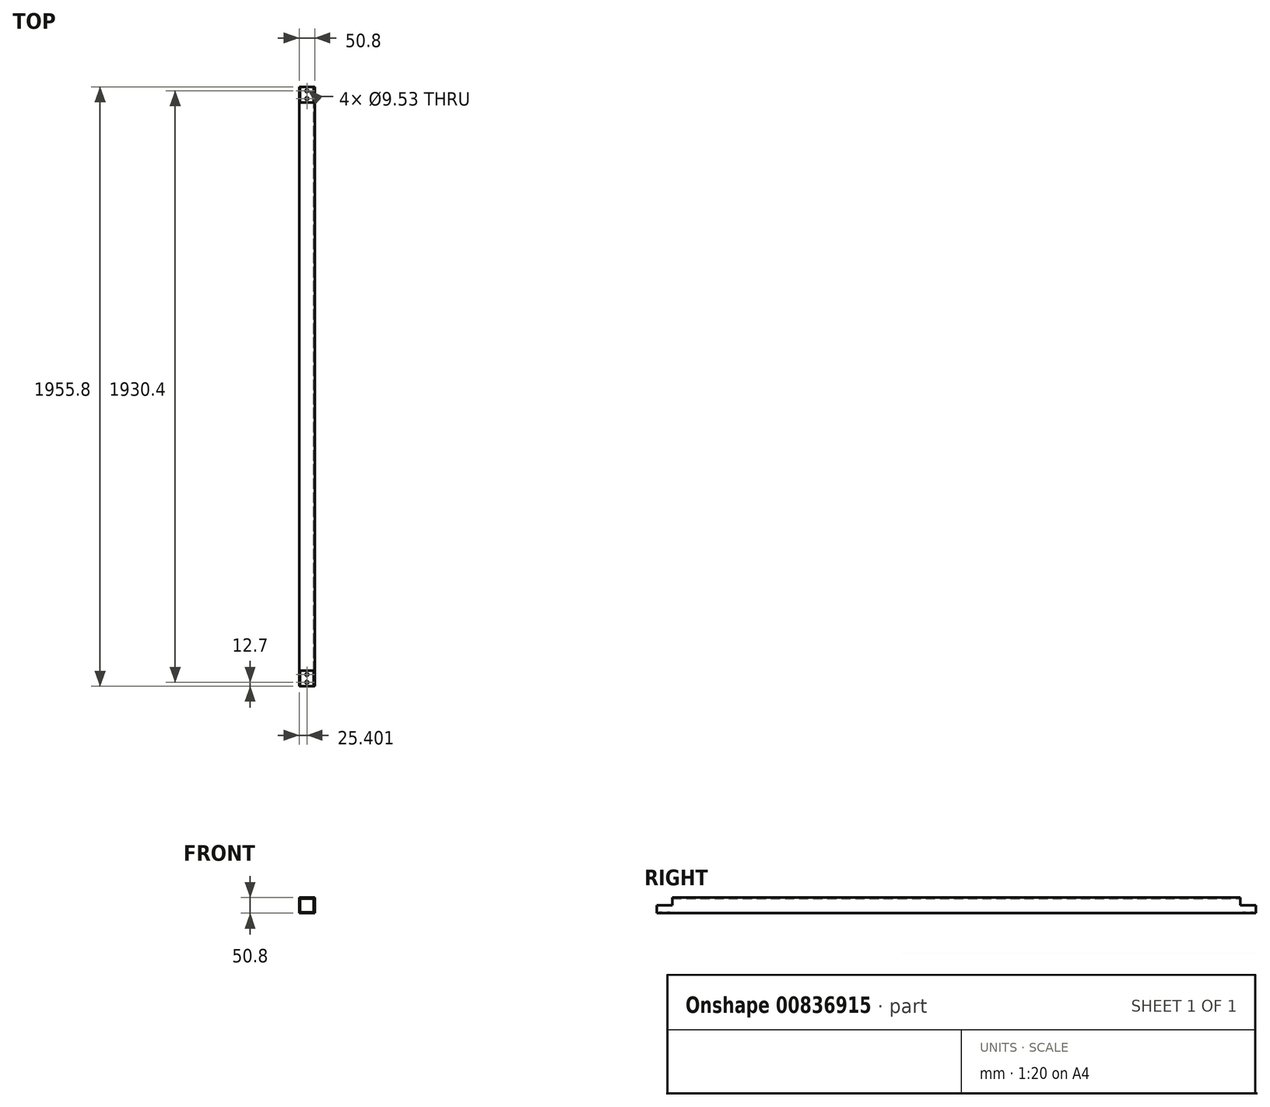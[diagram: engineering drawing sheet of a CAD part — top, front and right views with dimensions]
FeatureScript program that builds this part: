
annotation { "Feature Type Name" : "Feature", "Feature Type Description" : "" }
export const myFeature = defineFeature(function(context is Context, id is Id, definition is map)
    precondition{}
    {
        {
            var Q0;
            Q0=qCreatedBy(makeId("Front.planeOp"),FACE);
            var sketch = newSketch(context, id + "F0", { "sketchPlane" : qUnion([Q0])});
            skLineSegment(sketch, "E0.bottom", {"start": v(-6.18, -7.03) * mm, "end": v(44.62, -7.03) * mm});
            skLineSegment(sketch, "E0.top", {"start": v(-6.18, 43.77) * mm, "end": v(44.62, 43.77) * mm});
            skLineSegment(sketch, "E0.left", {"start": v(-6.18, -7.03) * mm, "end": v(-6.18, 43.77) * mm});
            skLineSegment(sketch, "E0.right", {"start": v(44.62, -7.03) * mm, "end": v(44.62, 43.77) * mm});
            skLineSegment(sketch, "E1.bottom", {"start": v(41.57, 40.72) * mm, "end": v(-3.13, 40.72) * mm});
            skLineSegment(sketch, "E1.top", {"start": v(41.57, -3.98) * mm, "end": v(-3.13, -3.98) * mm});
            skLineSegment(sketch, "E1.left", {"start": v(41.57, 40.72) * mm, "end": v(41.57, -3.98) * mm});
            skLineSegment(sketch, "E1.right", {"start": v(-3.13, 40.72) * mm, "end": v(-3.13, -3.98) * mm});
            skSolve(sketch);
        }
        {
            var Q0;
            Q0=makeQuery(id+"F0.imprint","IMPRINT",FACE,{"disambiguationData":[TD([[makeQuery(id+"F0.imprint","IMPRINT",EDGE,{"derivedFrom":sQuery(id+"F0.wireOp",EDGE,"E0.bottom")}),1.0]])]});
            extrude(context, id + "F1", {"entities" : qUnion([Q0]), "depth" : 1955.8 * mm, "offsetDistance" : 25.4 * mm, "symmetric" : true});
        }
        {
            var Q0;
            Q0=makeQuery(id+"F1.opExtrude","SWEPT_FACE",FACE,{"disambiguationData":[OSD([sQuery(id+"F0.wireOp",EDGE,"E1.top")])]});
            var sketch = newSketch(context, id + "F2", { "sketchPlane" : qUnion([Q0])});
            skCircle(sketch, "E2", {"center": v(19.22, -965.2) * mm, "radius": 4.76 * mm});
            skPoint(sketch, "E2.centerSnap0", {"position": v(19.22, -977.9) * mm});
            skCircle(sketch, "E3", {"center": v(19.22, -939.8) * mm, "radius": 4.76 * mm});
            skLineSegment(sketch, "E4", {"start": v(41.57, 0) * mm, "end": v(-3.13, 0) * mm, "construction": true});
            skPoint(sketch, "E5.MirrorP", {"position": v(19.22, 977.9) * mm});
            skCircle(sketch, "E6.MirrorC", {"center": v(19.22, 965.2) * mm, "radius": 4.76 * mm});
            skCircle(sketch, "E7.MirrorC", {"center": v(19.22, 939.8) * mm, "radius": 4.76 * mm});
            skSolve(sketch);
        }
        {
            var Q0;
            Q0 = qSketchRegion(id + "F2", true);
            extrude(context, id + "F3", {"entities" : qUnion([Q0]), "operationType" : NewBodyOperationType.REMOVE, "oppositeDirection" : true, "depth" : 25.4 * mm, "offsetDistance" : 25.4 * mm});
        }
        {
            var Q0;
            Q0=makeQuery(id+"F1.opExtrude","SWEPT_FACE",FACE,{"disambiguationData":[OSD([sQuery(id+"F0.wireOp",EDGE,"E0.top")])]});
            var sketch = newSketch(context, id + "F4", { "sketchPlane" : qUnion([Q0])});
            skLineSegment(sketch, "E8.bottom", {"start": v(44.62, -927.1) * mm, "end": v(-6.18, -927.1) * mm});
            skLineSegment(sketch, "E8.top", {"start": v(44.62, -1028.7) * mm, "end": v(-6.18, -1028.7) * mm});
            skLineSegment(sketch, "E8.left", {"start": v(44.62, -927.1) * mm, "end": v(44.62, -1028.7) * mm});
            skLineSegment(sketch, "E8.right", {"start": v(-6.18, -927.1) * mm, "end": v(-6.18, -1028.7) * mm});
            skPoint(sketch, "E8.middle", {"position": v(19.22, -977.9) * mm});
            skLineSegment(sketch, "E9.bottom", {"start": v(-6.18, 927.1) * mm, "end": v(44.62, 927.1) * mm});
            skLineSegment(sketch, "E9.top", {"start": v(-6.18, 1028.7) * mm, "end": v(44.62, 1028.7) * mm});
            skLineSegment(sketch, "E9.left", {"start": v(-6.18, 927.1) * mm, "end": v(-6.18, 1028.7) * mm});
            skLineSegment(sketch, "E9.right", {"start": v(44.62, 927.1) * mm, "end": v(44.62, 1028.7) * mm});
            skPoint(sketch, "E9.middle", {"position": v(19.22, 977.9) * mm});
            skSolve(sketch);
        }
        {
            var Q0;
            Q0 = qSketchRegion(id + "F4", true);
            var Q1;
            Q1=makeQuery(id+"F1.opExtrude","CAP_VERTEX",VERTEX,{"disambiguationData":[OSD([sQuery(id+"F0.wireOp",EDGE,"E1.top"),sQuery(id+"F0.wireOp",EDGE,"E1.right")])],"isStart":true});
            extrude(context, id + "F5", {"entities" : qUnion([Q0]), "operationType" : NewBodyOperationType.REMOVE, "oppositeDirection" : true, "depth" : 25.4 * mm, "endBoundEntityVertex" : qUnion([Q1]), "offsetDistance" : 25.4 * mm});
        }
    });
